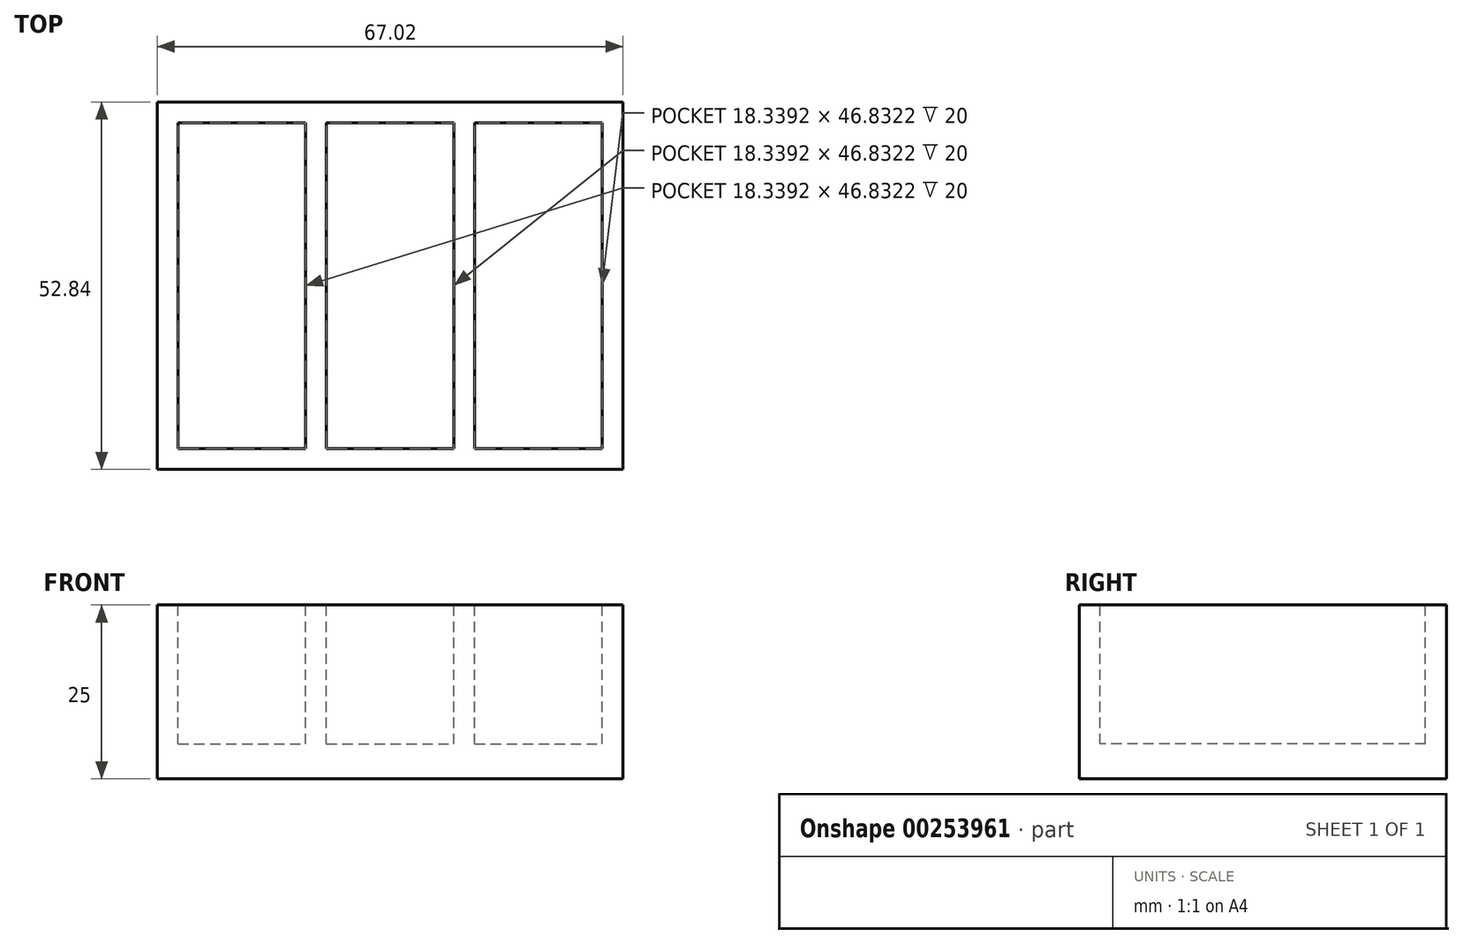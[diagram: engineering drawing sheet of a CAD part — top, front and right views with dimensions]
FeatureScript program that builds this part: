
annotation { "Feature Type Name" : "Feature", "Feature Type Description" : "" }
export const myFeature = defineFeature(function(context is Context, id is Id, definition is map)
    precondition{}
    {
        {
            var Q0;
            Q0=qCreatedBy(makeId("Top.planeOp"),FACE);
            var sketch = newSketch(context, id + "F0", { "sketchPlane" : qUnion([Q0])});
            skLineSegment(sketch, "E0.bottom", {"start": v(-33.5, 26.42) * mm, "end": v(33.5, 26.42) * mm});
            skLineSegment(sketch, "E0.top", {"start": v(-33.5, -26.42) * mm, "end": v(33.5, -26.42) * mm});
            skLineSegment(sketch, "E0.left", {"start": v(-33.5, 26.42) * mm, "end": v(-33.5, -26.42) * mm});
            skLineSegment(sketch, "E0.right", {"start": v(33.5, 26.42) * mm, "end": v(33.5, -26.42) * mm});
            skSolve(sketch);
        }
        {
            var Q0;
            Q0=makeQuery(id+"F0.imprint","IMPRINT",FACE,{"disambiguationData":[TD([[makeQuery(id+"F0.imprint","IMPRINT",EDGE,{"derivedFrom":sQuery(id+"F0.wireOp",EDGE,"E0.bottom")}),-1.0]])]});
            extrude(context, id + "F1", {"entities" : qUnion([Q0]), "depth" : 25 * mm});
        }
        {
            var Q0;
            Q0=makeQuery(id+"F1.opExtrude","CAP_FACE",FACE,{"disambiguationData":[OSD([sQuery(id+"F0.wireOp",EDGE,"E0.bottom"),sQuery(id+"F0.wireOp",EDGE,"E0.top"),sQuery(id+"F0.wireOp",EDGE,"E0.left"),sQuery(id+"F0.wireOp",EDGE,"E0.right")])],"isStart":false});
            var sketch = newSketch(context, id + "F2", { "sketchPlane" : qUnion([Q0])});
            skLineSegment(sketch, "E1.bottom", {"start": v(-30.5, 23.42) * mm, "end": v(-12.17, 23.42) * mm});
            skLineSegment(sketch, "E1.top", {"start": v(-30.5, -23.42) * mm, "end": v(-12.17, -23.42) * mm});
            skLineSegment(sketch, "E1.left", {"start": v(-30.5, 23.42) * mm, "end": v(-30.5, -23.42) * mm});
            skLineSegment(sketch, "E1.right", {"start": v(-12.17, 23.42) * mm, "end": v(-12.17, -23.42) * mm});
            skLineSegment(sketch, "E2.bottom", {"start": v(-9.17, 23.42) * mm, "end": v(9.17, 23.42) * mm});
            skLineSegment(sketch, "E2.top", {"start": v(-9.17, -23.42) * mm, "end": v(9.17, -23.42) * mm});
            skLineSegment(sketch, "E2.left", {"start": v(-9.17, 23.42) * mm, "end": v(-9.17, -23.42) * mm});
            skLineSegment(sketch, "E2.right", {"start": v(9.17, 23.42) * mm, "end": v(9.17, -23.42) * mm});
            skLineSegment(sketch, "E3.bottom", {"start": v(12.17, 23.42) * mm, "end": v(30.5, 23.42) * mm});
            skLineSegment(sketch, "E3.top", {"start": v(12.17, -23.42) * mm, "end": v(30.5, -23.42) * mm});
            skLineSegment(sketch, "E3.left", {"start": v(12.17, 23.42) * mm, "end": v(12.17, -23.42) * mm});
            skLineSegment(sketch, "E3.right", {"start": v(30.5, 23.42) * mm, "end": v(30.5, -23.42) * mm});
            skSolve(sketch);
        }
        {
            var Q0;
            Q0 = qSketchRegion(id + "F2", true);
            extrude(context, id + "F3", {"entities" : qUnion([Q0]), "operationType" : NewBodyOperationType.REMOVE, "oppositeDirection" : true, "depth" : 20 * mm});
        }
    });
